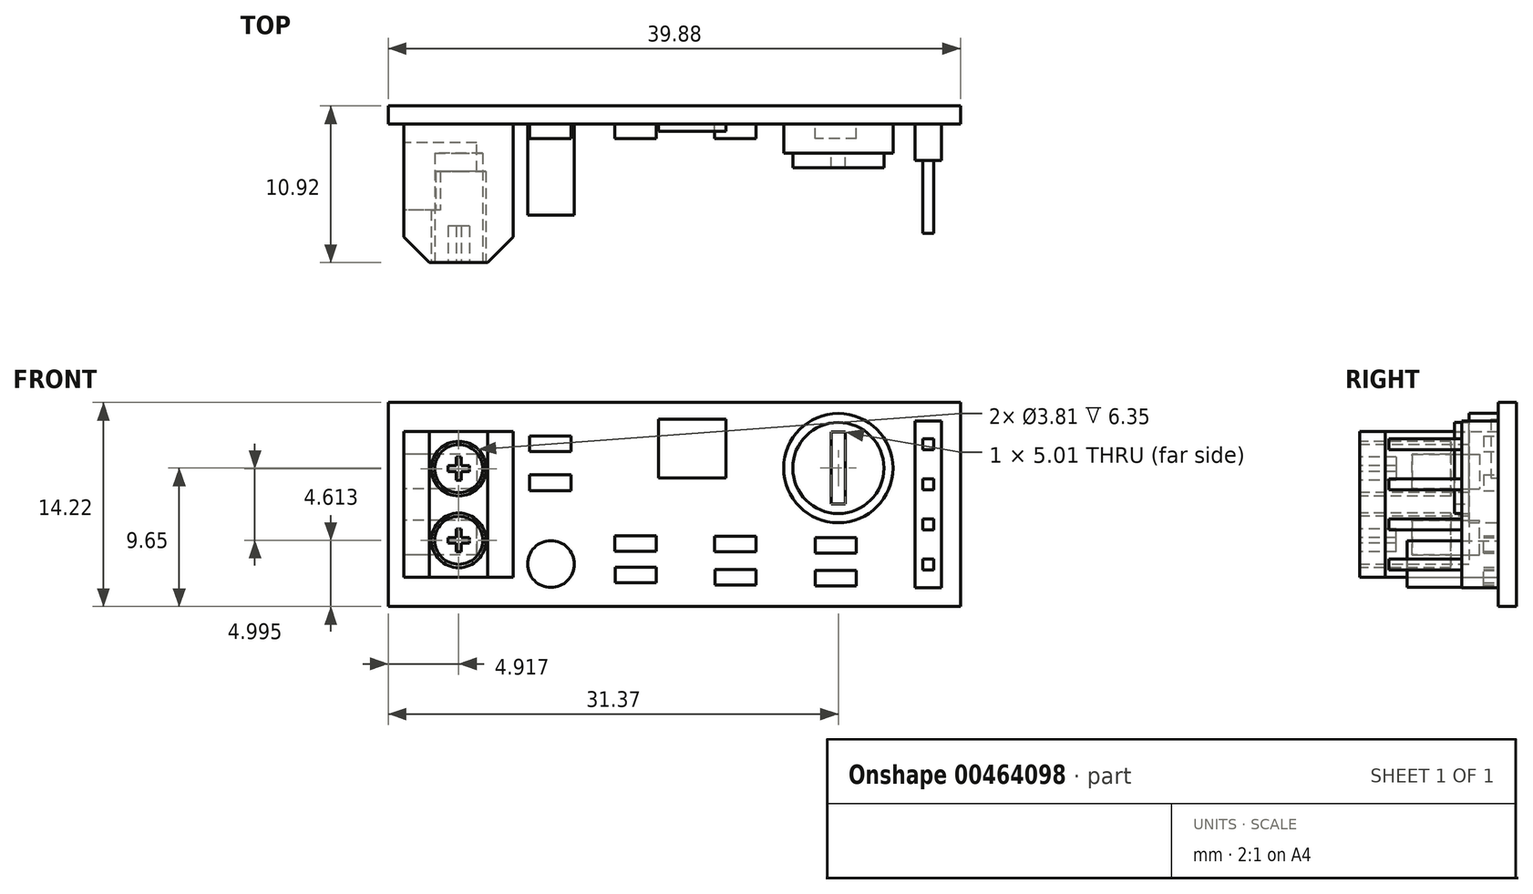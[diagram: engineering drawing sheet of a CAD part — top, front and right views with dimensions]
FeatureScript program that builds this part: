
annotation { "Feature Type Name" : "Feature", "Feature Type Description" : "" }
export const myFeature = defineFeature(function(context is Context, id is Id, definition is map)
    precondition{}
    {
        {
            var Q0;
            Q0=qCreatedBy(makeId("Front.planeOp"),FACE);
            var sketch = newSketch(context, id + "F0", { "sketchPlane" : qUnion([Q0])});
            skLineSegment(sketch, "E0.bottom", {"start": v(19.94, 7.11) * mm, "end": v(-19.94, 7.11) * mm});
            skLineSegment(sketch, "E0.top", {"start": v(19.94, -7.11) * mm, "end": v(-19.94, -7.11) * mm});
            skLineSegment(sketch, "E0.left", {"start": v(19.94, 7.11) * mm, "end": v(19.94, -7.11) * mm});
            skLineSegment(sketch, "E0.right", {"start": v(-19.94, 7.11) * mm, "end": v(-19.94, -7.11) * mm});
            skPoint(sketch, "E0.middle", {"position": v(0, 0) * mm});
            skSolve(sketch);
        }
        {
            var Q0;
            Q0 = qSketchRegion(id + "F0", true);
            extrude(context, id + "F1", {"entities" : qUnion([Q0]), "depth" : 1.27 * mm});
        }
        {
            var Q0;
            Q0=makeQuery(id+"F1.opExtrude","CAP_FACE",FACE,{"disambiguationData":[OSD([sQuery(id+"F0.wireOp",EDGE,"E0.bottom"),sQuery(id+"F0.wireOp",EDGE,"E0.top"),sQuery(id+"F0.wireOp",EDGE,"E0.left"),sQuery(id+"F0.wireOp",EDGE,"E0.right")])],"isStart":false});
            var sketch = newSketch(context, id + "F2", { "sketchPlane" : qUnion([Q0])});
            skLineSegment(sketch, "E1.bottom", {"start": v(-11.21, 5.08) * mm, "end": v(-18.83, 5.08) * mm});
            skLineSegment(sketch, "E1.top", {"start": v(-11.21, -5.08) * mm, "end": v(-18.83, -5.08) * mm});
            skLineSegment(sketch, "E1.left", {"start": v(-11.21, 5.08) * mm, "end": v(-11.21, -5.08) * mm});
            skLineSegment(sketch, "E1.right", {"start": v(-18.83, 5.08) * mm, "end": v(-18.83, -5.08) * mm});
            skPoint(sketch, "E1.middle", {"position": v(-15.02, 0) * mm});
            skSolve(sketch);
        }
        {
            var Q0;
            Q0 = qSketchRegion(id + "F2", true);
            extrude(context, id + "F3", {"entities" : qUnion([Q0]), "depth" : 9.65 * mm});
        }
        {
            var Q0;
            Q0=makeQuery(id+"F3.opExtrude","CAP_EDGE",EDGE,{"disambiguationData":[OSD([sQuery(id+"F2.wireOp",EDGE,"E1.right")])],"isStart":false});
            var Q1;
            Q1=makeQuery(id+"F3.opExtrude","CAP_EDGE",EDGE,{"disambiguationData":[OSD([sQuery(id+"F2.wireOp",EDGE,"E1.left")])],"isStart":false});
            chamfer(context, id + "F4", {"entities" : qUnion([Q0, Q1]), "width" : 1.78 * mm, "tangentPropagation" : true});
        }
        {
            var Q0;
            Q0=makeQuery(id+"F3.opExtrude","CAP_FACE",FACE,{"disambiguationData":[OSD([sQuery(id+"F2.wireOp",EDGE,"E1.bottom"),sQuery(id+"F2.wireOp",EDGE,"E1.top"),sQuery(id+"F2.wireOp",EDGE,"E1.left"),sQuery(id+"F2.wireOp",EDGE,"E1.right")])],"isStart":false});
            var sketch = newSketch(context, id + "F5", { "sketchPlane" : qUnion([Q0])});
            skCircle(sketch, "E2", {"center": v(-15.02, 2.5) * mm, "radius": 1.9 * mm});
            skPoint(sketch, "E2.centerSnap0", {"position": v(-15.02, 5.08) * mm});
            skCircle(sketch, "E3.MirrorC", {"center": v(-15.02, -2.5) * mm, "radius": 1.9 * mm});
            skSolve(sketch);
        }
        {
            var Q0;
            Q0 = qSketchRegion(id + "F5", true);
            extrude(context, id + "F6", {"entities" : qUnion([Q0]), "operationType" : NewBodyOperationType.REMOVE, "oppositeDirection" : true, "depth" : 6.35 * mm});
        }
        {
            var Q0;
            Q0=makeQuery(id+"F3.opExtrude","SWEPT_FACE",FACE,{"disambiguationData":[OSD([sQuery(id+"F2.wireOp",EDGE,"E1.right")])]});
            var sketch = newSketch(context, id + "F7", { "sketchPlane" : qUnion([Q0])});
            skLineSegment(sketch, "E4.bottom", {"start": v(7.25, 3.51) * mm, "end": v(2.56, 3.51) * mm});
            skLineSegment(sketch, "E4.top", {"start": v(7.25, 1.1) * mm, "end": v(2.56, 1.1) * mm});
            skLineSegment(sketch, "E4.left", {"start": v(7.25, 3.51) * mm, "end": v(7.25, 1.1) * mm});
            skLineSegment(sketch, "E4.right", {"start": v(2.56, 3.51) * mm, "end": v(2.56, 1.1) * mm});
            skPoint(sketch, "E4.middle", {"position": v(4.9, 2.3) * mm});
            skLineSegment(sketch, "E5.MirrorCS", {"start": v(2.56, -3.51) * mm, "end": v(2.56, -1.1) * mm});
            skLineSegment(sketch, "E6.MirrorCS", {"start": v(7.25, -1.1) * mm, "end": v(2.56, -1.1) * mm});
            skLineSegment(sketch, "E7.MirrorCS", {"start": v(7.25, -3.51) * mm, "end": v(2.56, -3.51) * mm});
            skLineSegment(sketch, "E8.MirrorCS", {"start": v(7.25, -3.51) * mm, "end": v(7.25, -1.1) * mm});
            skSolve(sketch);
        }
        {
            var Q0;
            Q0 = qSketchRegion(id + "F7", true);
            extrude(context, id + "F8", {"entities" : qUnion([Q0]), "operationType" : NewBodyOperationType.REMOVE, "oppositeDirection" : true, "depth" : 5.08 * mm});
        }
        {
            var Q0;
            Q0=makeQuery(id+"F3.opExtrude","CAP_FACE",FACE,{"disambiguationData":[OSD([sQuery(id+"F2.wireOp",EDGE,"E1.bottom"),sQuery(id+"F2.wireOp",EDGE,"E1.top"),sQuery(id+"F2.wireOp",EDGE,"E1.left"),sQuery(id+"F2.wireOp",EDGE,"E1.right")])],"isStart":false});
            var sketch = newSketch(context, id + "F9", { "sketchPlane" : qUnion([Q0])});
            skCircle(sketch, "E9", {"center": v(-15.02, 2.5) * mm, "radius": 1.67 * mm});
            skSolve(sketch);
        }
        {
            var Q0;
            Q0 = qSketchRegion(id + "F9", true);
            extrude(context, id + "F10", {"entities" : qUnion([Q0]), "oppositeDirection" : true, "depth" : 7.62 * mm});
        }
        {
            var Q0;
            Q0=makeQuery(id+"F10.opExtrude","CAP_FACE",FACE,{"disambiguationData":[OSD([sQuery(id+"F9.wireOp",EDGE,"E9")])],"isStart":true});
            var sketch = newSketch(context, id + "F11", { "sketchPlane" : qUnion([Q0])});
            skLineSegment(sketch, "E10.bottom", {"start": v(-14.84, 3.3) * mm, "end": v(-15.2, 3.3) * mm});
            skLineSegment(sketch, "E10.top", {"start": v(-14.84, 1.7) * mm, "end": v(-15.2, 1.7) * mm});
            skLineSegment(sketch, "E10.left", {"start": v(-14.84, 3.3) * mm, "end": v(-14.84, 1.7) * mm});
            skLineSegment(sketch, "E10.right", {"start": v(-15.2, 3.3) * mm, "end": v(-15.2, 1.7) * mm});
            skPoint(sketch, "E10.middle", {"position": v(-15.02, 2.5) * mm});
            skLineSegment(sketch, "E11.bottom", {"start": v(-14.29, 2.7) * mm, "end": v(-15.76, 2.7) * mm});
            skLineSegment(sketch, "E11.top", {"start": v(-14.29, 2.3) * mm, "end": v(-15.76, 2.3) * mm});
            skLineSegment(sketch, "E11.left", {"start": v(-14.29, 2.7) * mm, "end": v(-14.29, 2.3) * mm});
            skLineSegment(sketch, "E11.right", {"start": v(-15.76, 2.7) * mm, "end": v(-15.76, 2.3) * mm});
            skSolve(sketch);
        }
        {
            var Q0;
            Q0 = qSketchRegion(id + "F11", true);
            extrude(context, id + "F12", {"entities" : qUnion([Q0]), "operationType" : NewBodyOperationType.REMOVE, "oppositeDirection" : true, "depth" : 2.54 * mm});
        }
        {
            var Q0;
            Q0=makeQuery(id+"F10.opExtrude","SWEPT_BODY",BODY,{"disambiguationData":[OSD([sQuery(id+"F9.wireOp",EDGE,"E9")])]});
            var Q1;
            Q1=qCreatedBy(makeId("Top.planeOp"),FACE);
            mirror(context, id + "F13", {"entities" : qUnion([Q0]), "mirrorPlane" : qUnion([Q1])});
        }
        {
            var Q0;
            Q0=makeQuery(id+"F1.opExtrude","CAP_FACE",FACE,{"disambiguationData":[OSD([sQuery(id+"F0.wireOp",EDGE,"E0.bottom"),sQuery(id+"F0.wireOp",EDGE,"E0.top"),sQuery(id+"F0.wireOp",EDGE,"E0.left"),sQuery(id+"F0.wireOp",EDGE,"E0.right")])],"isStart":false});
            var sketch = newSketch(context, id + "F14", { "sketchPlane" : qUnion([Q0])});
            skLineSegment(sketch, "E12.bottom", {"start": v(18.62, 5.81) * mm, "end": v(16.77, 5.81) * mm});
            skLineSegment(sketch, "E12.top", {"start": v(18.62, -5.81) * mm, "end": v(16.77, -5.81) * mm});
            skLineSegment(sketch, "E12.left", {"start": v(18.62, 5.81) * mm, "end": v(18.62, -5.81) * mm});
            skLineSegment(sketch, "E12.right", {"start": v(16.77, 5.81) * mm, "end": v(16.77, -5.81) * mm});
            skPoint(sketch, "E12.middle", {"position": v(17.7, 0) * mm});
            skSolve(sketch);
        }
        {
            var Q0;
            Q0=makeQuery(id+"F14.imprint","IMPRINT",FACE,{"disambiguationData":[TD([[makeQuery(id+"F14.imprint","IMPRINT",EDGE,{"derivedFrom":sQuery(id+"F14.wireOp",EDGE,"E12.bottom")}),1.0]])]});
            extrude(context, id + "F15", {"entities" : qUnion([Q0]), "depth" : 2.54 * mm});
        }
        {
            var Q0;
            Q0=makeQuery(id+"F15.opExtrude","CAP_FACE",FACE,{"disambiguationData":[OSD([sQuery(id+"F14.wireOp",EDGE,"E12.bottom"),sQuery(id+"F14.wireOp",EDGE,"E12.top"),sQuery(id+"F14.wireOp",EDGE,"E12.left"),sQuery(id+"F14.wireOp",EDGE,"E12.right")])],"isStart":false});
            var sketch = newSketch(context, id + "F16", { "sketchPlane" : qUnion([Q0])});
            skLineSegment(sketch, "E13.bottom", {"start": v(18.08, -1.78) * mm, "end": v(17.31, -1.78) * mm});
            skLineSegment(sketch, "E13.top", {"start": v(18.08, -1.02) * mm, "end": v(17.31, -1.02) * mm});
            skLineSegment(sketch, "E13.left", {"start": v(18.08, -1.78) * mm, "end": v(18.08, -1.02) * mm});
            skLineSegment(sketch, "E13.right", {"start": v(17.31, -1.78) * mm, "end": v(17.31, -1.02) * mm});
            skPoint(sketch, "E13.middle", {"position": v(19.12, -1.39) * mm});
            skLineSegment(sketch, "E14.bottom", {"start": v(18.08, -3.81) * mm, "end": v(17.31, -3.81) * mm});
            skLineSegment(sketch, "E14.top", {"start": v(18.08, -4.57) * mm, "end": v(17.31, -4.57) * mm});
            skLineSegment(sketch, "E14.left", {"start": v(18.08, -3.81) * mm, "end": v(18.08, -4.57) * mm});
            skLineSegment(sketch, "E14.right", {"start": v(17.31, -3.81) * mm, "end": v(17.31, -4.57) * mm});
            skPoint(sketch, "E14.middle", {"position": v(19.12, -4.2) * mm});
            skLineSegment(sketch, "E15.MirrorCS", {"start": v(18.08, 1.02) * mm, "end": v(17.31, 1.02) * mm});
            skLineSegment(sketch, "E16.MirrorCS", {"start": v(18.08, 1.78) * mm, "end": v(18.08, 1.02) * mm});
            skLineSegment(sketch, "E17.MirrorCS", {"start": v(18.08, 1.78) * mm, "end": v(17.31, 1.78) * mm});
            skLineSegment(sketch, "E18.MirrorCS", {"start": v(17.31, 1.78) * mm, "end": v(17.31, 1.02) * mm});
            skLineSegment(sketch, "E19.MirrorCS", {"start": v(18.08, 3.81) * mm, "end": v(17.31, 3.81) * mm});
            skLineSegment(sketch, "E20.MirrorCS", {"start": v(18.08, 3.81) * mm, "end": v(18.08, 4.57) * mm});
            skLineSegment(sketch, "E21.MirrorCS", {"start": v(18.08, 4.57) * mm, "end": v(17.31, 4.57) * mm});
            skLineSegment(sketch, "E22.MirrorCS", {"start": v(17.31, 3.8) * mm, "end": v(17.31, 4.57) * mm});
            skLineSegment(sketch, "E23", {"start": v(17.7, 5.81) * mm, "end": v(17.7, -5.81) * mm, "construction": true});
            skSolve(sketch);
        }
        {
            var Q0;
            Q0 = qSketchRegion(id + "F16", true);
            extrude(context, id + "F17", {"entities" : qUnion([Q0]), "depth" : 5.08 * mm});
        }
        {
            var Q0;
            Q0=makeQuery(id+"F1.opExtrude","CAP_FACE",FACE,{"disambiguationData":[OSD([sQuery(id+"F0.wireOp",EDGE,"E0.bottom"),sQuery(id+"F0.wireOp",EDGE,"E0.top"),sQuery(id+"F0.wireOp",EDGE,"E0.left"),sQuery(id+"F0.wireOp",EDGE,"E0.right")])],"isStart":false});
            var sketch = newSketch(context, id + "F18", { "sketchPlane" : qUnion([Q0])});
            skCircle(sketch, "E24", {"center": v(-8.6, -4.15) * mm, "radius": 1.63 * mm});
            skSolve(sketch);
        }
        {
            var Q0;
            Q0 = qSketchRegion(id + "F18", true);
            extrude(context, id + "F19", {"entities" : qUnion([Q0]), "depth" : 6.35 * mm});
        }
        {
            var Q0;
            Q0=makeQuery(id+"F1.opExtrude","CAP_FACE",FACE,{"disambiguationData":[OSD([sQuery(id+"F0.wireOp",EDGE,"E0.bottom"),sQuery(id+"F0.wireOp",EDGE,"E0.top"),sQuery(id+"F0.wireOp",EDGE,"E0.left"),sQuery(id+"F0.wireOp",EDGE,"E0.right")])],"isStart":false});
            var sketch = newSketch(context, id + "F20", { "sketchPlane" : qUnion([Q0])});
            skLineSegment(sketch, "E25.bottom", {"start": v(3.58, 5.95) * mm, "end": v(-1.1, 5.95) * mm});
            skLineSegment(sketch, "E25.top", {"start": v(3.58, 1.86) * mm, "end": v(-1.1, 1.86) * mm});
            skLineSegment(sketch, "E25.left", {"start": v(3.58, 5.95) * mm, "end": v(3.58, 1.86) * mm});
            skLineSegment(sketch, "E25.right", {"start": v(-1.1, 5.95) * mm, "end": v(-1.1, 1.86) * mm});
            skPoint(sketch, "E25.middle", {"position": v(1.24, 3.9) * mm});
            skSolve(sketch);
        }
        {
            var Q0;
            Q0 = qSketchRegion(id + "F20", true);
            extrude(context, id + "F21", {"entities" : qUnion([Q0]), "depth" : 0.5 * mm});
        }
        {
            var Q0;
            Q0=makeQuery(id+"F1.opExtrude","CAP_FACE",FACE,{"disambiguationData":[OSD([sQuery(id+"F0.wireOp",EDGE,"E0.bottom"),sQuery(id+"F0.wireOp",EDGE,"E0.top"),sQuery(id+"F0.wireOp",EDGE,"E0.left"),sQuery(id+"F0.wireOp",EDGE,"E0.right")])],"isStart":false});
            var sketch = newSketch(context, id + "F22", { "sketchPlane" : qUnion([Q0])});
            skCircle(sketch, "E26", {"center": v(11.43, 2.54) * mm, "radius": 3.81 * mm});
            skSolve(sketch);
        }
        {
            var Q0;
            Q0=makeQuery(id+"F22.imprint","IMPRINT",FACE,{"disambiguationData":[TD([[makeQuery(id+"F22.imprint","IMPRINT",EDGE,{"derivedFrom":sQuery(id+"F22.wireOp",EDGE,"E26")}),1.0]])]});
            extrude(context, id + "F23", {"entities" : qUnion([Q0]), "depth" : 2.03 * mm});
        }
        {
            var Q0;
            Q0=makeQuery(id+"F23.opExtrude","CAP_FACE",FACE,{"disambiguationData":[OSD([sQuery(id+"F22.wireOp",EDGE,"E26")])],"isStart":false});
            var sketch = newSketch(context, id + "F24", { "sketchPlane" : qUnion([Q0])});
            skCircle(sketch, "E27", {"center": v(11.43, 2.54) * mm, "radius": 3.17 * mm});
            skLineSegment(sketch, "E28.bottom", {"start": v(10.93, 5.04) * mm, "end": v(11.93, 5.04) * mm});
            skLineSegment(sketch, "E28.top", {"start": v(10.93, 0.04) * mm, "end": v(11.93, 0.04) * mm});
            skLineSegment(sketch, "E28.left", {"start": v(10.93, 5.04) * mm, "end": v(10.93, 0.04) * mm});
            skLineSegment(sketch, "E28.right", {"start": v(11.93, 5.04) * mm, "end": v(11.93, 0.04) * mm});
            skSolve(sketch);
        }
        {
            var Q0;
            Q0 = qSketchRegion(id + "F24", true);
            extrude(context, id + "F25", {"entities" : qUnion([Q0]), "depth" : 1.02 * mm});
        }
        {
            var Q0;
            Q0=makeQuery(id+"F1.opExtrude","CAP_FACE",FACE,{"disambiguationData":[OSD([sQuery(id+"F0.wireOp",EDGE,"E0.bottom"),sQuery(id+"F0.wireOp",EDGE,"E0.top"),sQuery(id+"F0.wireOp",EDGE,"E0.left"),sQuery(id+"F0.wireOp",EDGE,"E0.right")])],"isStart":false});
            var sketch = newSketch(context, id + "F26", { "sketchPlane" : qUnion([Q0])});
            skLineSegment(sketch, "E29.bottom", {"start": v(-7.2, 4.77) * mm, "end": v(-10.08, 4.77) * mm});
            skLineSegment(sketch, "E29.top", {"start": v(-7.2, 3.7) * mm, "end": v(-10.08, 3.7) * mm});
            skLineSegment(sketch, "E29.left", {"start": v(-7.2, 4.77) * mm, "end": v(-7.2, 3.7) * mm});
            skLineSegment(sketch, "E29.right", {"start": v(-10.08, 4.77) * mm, "end": v(-10.08, 3.7) * mm});
            skPoint(sketch, "E29.middle", {"position": v(-8.64, 4.23) * mm});
            skLineSegment(sketch, "E30.bottom", {"start": v(-7.2, 2.07) * mm, "end": v(-10.08, 2.07) * mm});
            skLineSegment(sketch, "E30.top", {"start": v(-7.2, 0.97) * mm, "end": v(-10.08, 0.97) * mm});
            skLineSegment(sketch, "E30.left", {"start": v(-7.2, 2.07) * mm, "end": v(-7.2, 0.97) * mm});
            skLineSegment(sketch, "E30.right", {"start": v(-10.08, 2.07) * mm, "end": v(-10.08, 0.97) * mm});
            skPoint(sketch, "E30.middle", {"position": v(-8.64, 1.52) * mm});
            skPoint(sketch, "E30.cornerSnap0", {"position": v(-7.2, 4.23) * mm});
            skLineSegment(sketch, "E31.bottom", {"start": v(-1.27, -3.24) * mm, "end": v(-4.15, -3.24) * mm});
            skLineSegment(sketch, "E31.top", {"start": v(-1.27, -2.17) * mm, "end": v(-4.15, -2.17) * mm});
            skLineSegment(sketch, "E31.left", {"start": v(-1.27, -3.24) * mm, "end": v(-1.27, -2.17) * mm});
            skLineSegment(sketch, "E31.right", {"start": v(-4.15, -3.24) * mm, "end": v(-4.15, -2.17) * mm});
            skPoint(sketch, "E31.middle", {"position": v(-2.71, -2.7) * mm});
            skLineSegment(sketch, "E32.bottom", {"start": v(-1.25, -5.44) * mm, "end": v(-4.12, -5.44) * mm});
            skLineSegment(sketch, "E32.top", {"start": v(-1.25, -4.36) * mm, "end": v(-4.12, -4.36) * mm});
            skLineSegment(sketch, "E32.left", {"start": v(-1.25, -5.44) * mm, "end": v(-1.25, -4.36) * mm});
            skLineSegment(sketch, "E32.right", {"start": v(-4.12, -5.44) * mm, "end": v(-4.12, -4.36) * mm});
            skPoint(sketch, "E32.middle", {"position": v(-2.69, -4.9) * mm});
            skLineSegment(sketch, "E33.bottom", {"start": v(5.68, -3.3) * mm, "end": v(2.8, -3.3) * mm});
            skLineSegment(sketch, "E33.top", {"start": v(5.68, -2.22) * mm, "end": v(2.8, -2.22) * mm});
            skLineSegment(sketch, "E33.left", {"start": v(5.68, -3.3) * mm, "end": v(5.68, -2.22) * mm});
            skLineSegment(sketch, "E33.right", {"start": v(2.8, -3.3) * mm, "end": v(2.8, -2.22) * mm});
            skPoint(sketch, "E33.middle", {"position": v(4.24, -2.76) * mm});
            skLineSegment(sketch, "E34.bottom", {"start": v(5.7, -5.62) * mm, "end": v(2.83, -5.62) * mm});
            skLineSegment(sketch, "E34.top", {"start": v(5.7, -4.55) * mm, "end": v(2.83, -4.55) * mm});
            skLineSegment(sketch, "E34.left", {"start": v(5.7, -5.62) * mm, "end": v(5.7, -4.55) * mm});
            skLineSegment(sketch, "E34.right", {"start": v(2.83, -5.62) * mm, "end": v(2.83, -4.55) * mm});
            skPoint(sketch, "E34.middle", {"position": v(4.27, -5.09) * mm});
            skLineSegment(sketch, "E35.bottom", {"start": v(12.69, -3.38) * mm, "end": v(9.8, -3.38) * mm});
            skLineSegment(sketch, "E35.top", {"start": v(12.69, -2.3) * mm, "end": v(9.8, -2.3) * mm});
            skLineSegment(sketch, "E35.left", {"start": v(12.69, -3.38) * mm, "end": v(12.69, -2.3) * mm});
            skLineSegment(sketch, "E35.right", {"start": v(9.8, -3.38) * mm, "end": v(9.8, -2.3) * mm});
            skPoint(sketch, "E35.middle", {"position": v(11.25, -2.84) * mm});
            skLineSegment(sketch, "E36.bottom", {"start": v(12.69, -5.68) * mm, "end": v(9.8, -5.68) * mm});
            skLineSegment(sketch, "E36.top", {"start": v(12.69, -4.6) * mm, "end": v(9.8, -4.6) * mm});
            skLineSegment(sketch, "E36.left", {"start": v(12.69, -5.68) * mm, "end": v(12.69, -4.6) * mm});
            skLineSegment(sketch, "E36.right", {"start": v(9.8, -5.68) * mm, "end": v(9.8, -4.6) * mm});
            skPoint(sketch, "E36.middle", {"position": v(11.25, -5.14) * mm});
            skSolve(sketch);
        }
        {
            var Q0;
            Q0 = qSketchRegion(id + "F26", true);
            extrude(context, id + "F27", {"entities" : qUnion([Q0]), "depth" : 1.02 * mm});
        }
    });
